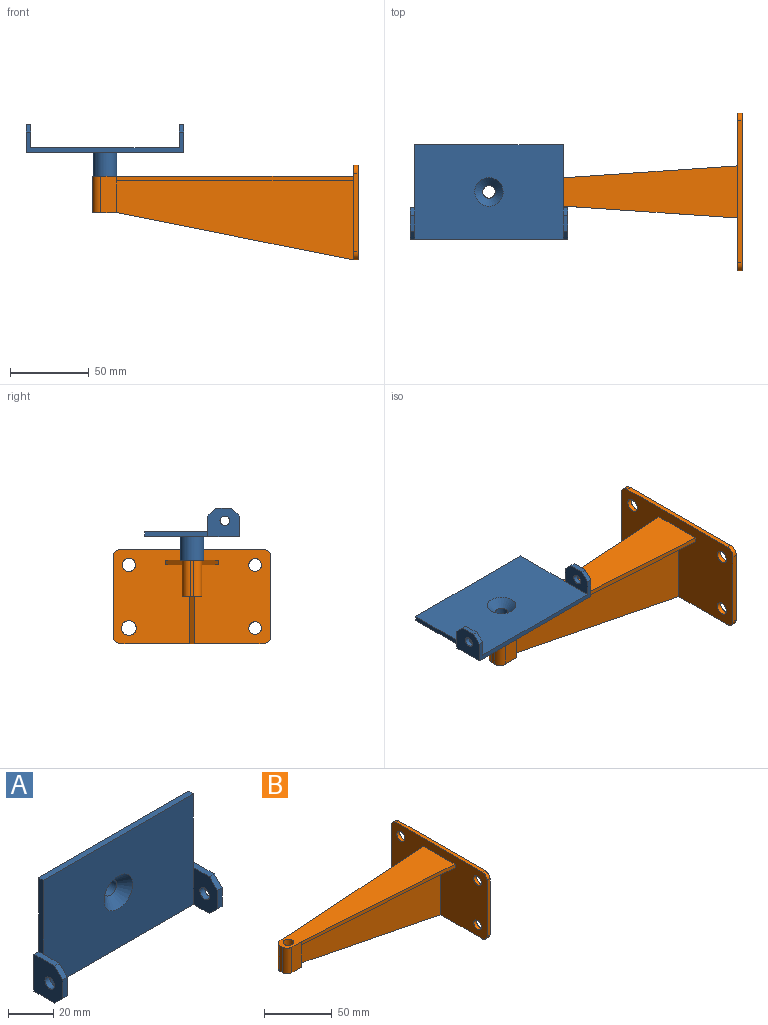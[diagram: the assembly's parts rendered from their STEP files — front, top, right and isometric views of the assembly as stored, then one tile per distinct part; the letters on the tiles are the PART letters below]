
ASSEMBLY  parts=2 mates=1
PART A: 24 faces, bbox 100x33x60 mm
  f0: plane 94x60mm, normal (0,-1,0), area 5385.5mm2, adj f1,f4,f5,f6,f10,f12,f23
  f1: plane 100x13mm, normal (0,0,-1), area 360mm2, adj f0,f2,f8,f9,f10,f12,f16,f17
  f2: plane 20x18mm, normal (1,0,0), area 306.7mm2, adj f1,f3,f9,f13,f14,f16,f18
  f3: plane 13x3mm, normal (0,0,1), area 39mm2, adj f2,f4,f9,f12,f18
  f4: plane 40x3mm, normal (1,0,0), area 120mm2, adj f0,f3,f5,f9
  f5: plane 94x3mm, normal (0,0,1), area 282mm2, adj f0,f4,f6,f9
  f6: plane 40x3mm, normal (-1,0,0), area 120mm2, adj f0,f5,f7,f9
  f7: plane 13x3mm, normal (0,0,1), area 39mm2, adj f6,f8,f9,f10,f19
  f8: plane 20x18mm, normal (-1,0,0), area 306.7mm2, adj f1,f7,f9,f11,f15,f17,f19
  f9: plane 100x60mm, normal (0,1,0), area 5583.3mm2, adj f1,f2,f3,f4,f5,f6,f7,f8
  f10: plane 20x15mm, normal (1,0,0), area 246.7mm2, adj f0,f1,f7,f11,f15,f17,f19
  f11: plane 10x3mm, normal (0,-1,0), area 30mm2, adj f8,f10,f17,f19
  f12: plane 20x15mm, normal (-1,0,0), area 246.7mm2, adj f0,f1,f3,f13,f14,f16,f18
  f13: plane 10x3mm, normal (0,-1,0), area 30mm2, adj f2,f12,f16,f18
  f14: cylinder r=3mm len=6mm, axis (-1,0,0), area 56.5mm2, adj f2,f12
  f15: cylinder r=3mm len=6mm, axis (-1,0,0), area 56.5mm2, adj f8,f10
  f16: plane 5x5mm, normal (0,-0.71,-0.71), area 21.2mm2, adj f1,f2,f12,f13
  f17: plane 5x5mm, normal (0,-0.71,-0.71), area 21.2mm2, adj f1,f8,f10,f11
  f18: plane 5x5mm, normal (0,-0.71,0.71), area 21.2mm2, adj f2,f3,f12,f13
  f19: plane 5x5mm, normal (0,-0.71,0.71), area 21.2mm2, adj f7,f8,f10,f11
  f20: cylinder r=7.5mm len=15mm, axis (0,-1,0), area 706.9mm2, adj f9,f21
  f21: plane 15x15mm, normal (0,1,0), area 126.4mm2, adj f20,f22
  f22: cylinder r=4mm len=13mm, axis (0,1,0), area 326.7mm2, adj f21,f23
  f23: cone r=4mm half-angle=45deg, axis (0,-1,0), area 288.8mm2, adj f0,f22
PART B: 31 faces, bbox 168x100x60 mm
  f0: plane 150x30mm, normal (-0.2,0,-0.98), area 458.9mm2, adj f1,f2,f9,f28
  f1: plane 150x50mm, normal (0,-1,0), area 5250mm2, adj f0,f7,f8,f22
  f2: plane 150x50mm, normal (0,1,0), area 5250mm2, adj f0,f3,f8,f24
  f3: plane 150x15mm, normal (0,0,-1), area 1477.9mm2, adj f2,f5,f8,f24
  f4: plane 150x10.27mm, normal (-0.07,-1,0), area 451.1mm2, adj f6,f7,f8,f23
  f5: plane 150x10.3mm, normal (-0.07,1,0), area 451.1mm2, adj f3,f6,f8,f25
  f6: plane 165x33mm, normal (0,0,1), area 3533.2mm2, adj f4,f5,f8,f23,f25,f26,f27,f29
  f7: plane 150x15mm, normal (0,0,-1), area 1479.8mm2, adj f1,f4,f8,f22
  f8: plane 100x60mm, normal (-1,0,0), area 5504.6mm2, adj f1,f2,f3,f4,f5,f6,f7,f9
  f9: plane 90x3mm, normal (0,0,-1), area 270mm2, adj f0,f8,f18,f20,f21
  f10: plane 50x3mm, normal (0,1,0), area 150mm2, adj f8,f11,f20,f21
  f11: cylinder r=5mm len=5mm, axis (-1,0,0), area 23.6mm2, adj f8,f10,f12,f20
  f12: plane 90x3mm, normal (0,0,1), area 270mm2, adj f8,f11,f13,f20
  f13: cylinder r=5mm len=5mm, axis (-1,0,0), area 23.6mm2, adj f8,f12,f14,f20
  f14: plane 50x3mm, normal (0,-1,0), area 150mm2, adj f8,f13,f18,f20
  f15: cylinder r=4.69mm len=9.37mm, axis (-1,0,0), area 88.3mm2, adj f8,f20
  f16: cylinder r=4mm len=8mm, axis (-1,0,0), area 75.4mm2, adj f8,f20
  f17: cylinder r=4.2mm len=8.4mm, axis (-1,0,0), area 79.2mm2, adj f8,f20
  f18: cylinder r=5mm len=5mm, axis (-1,0,0), area 23.6mm2, adj f8,f9,f14,f20
  f19: cylinder r=4mm len=8mm, axis (-1,0,0), area 75.4mm2, adj f8,f20
  f20: plane 100x60mm, normal (1,0,0), area 5753.6mm2, adj f9,f10,f11,f12,f13,f14,f15,f16
  f21: cylinder r=5mm len=5mm, axis (-1,0,0), area 23.6mm2, adj f8,f9,f10,f20
  f22: plane 20x4.73mm, normal (1,0,0), area 94.6mm2, adj f1,f7,f23,f28
  f23: plane 23x10mm, normal (0,-1,0), area 230mm2, adj f4,f6,f22,f28,f30
  f24: plane 20x4.7mm, normal (1,0,0), area 94.1mm2, adj f2,f3,f25,f28
  f25: plane 23x10mm, normal (0,1,0), area 230mm2, adj f5,f6,f24,f28,f29
  f26: plane 23x2.44mm, normal (-1,0,0), area 56mm2, adj f6,f28,f29,f30
  f27: cylinder r=4mm len=23mm, axis (0,0,1), area 578.1mm2, adj f6,f28
  f28: plane 15x12.44mm, normal (0,0,-1), area 125.5mm2, adj f0,f22,f23,f24,f25,f26,f27,f29
  f29: cylinder r=5mm len=23mm, axis (0,0,-1), area 180.6mm2, adj f6,f25,f26,f28
  f30: cylinder r=5mm len=23mm, axis (0,0,1), area 180.6mm2, adj f6,f23,f26,f28
PLACE A rot(axis=(-1,0,0),90deg) t=(-171.92,-31.35,73.79)mm
PLACE B t=(-14.59,-29.83,5.79)mm fixed
MATE revolute A.f20 <-> B.f27  axis (0,0,-1) through (-171.92,-31.35,58.79)mm
